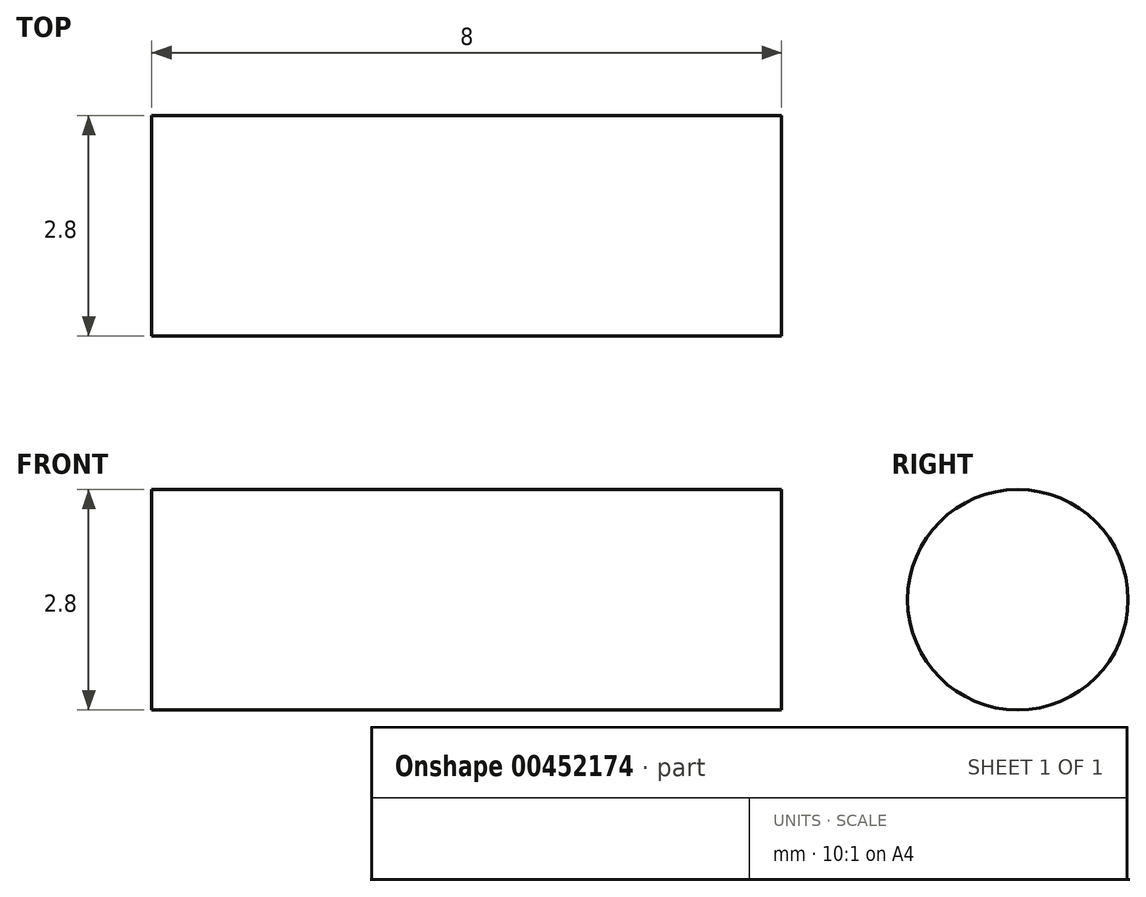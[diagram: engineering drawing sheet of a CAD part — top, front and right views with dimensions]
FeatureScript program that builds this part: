
annotation { "Feature Type Name" : "Feature", "Feature Type Description" : "" }
export const myFeature = defineFeature(function(context is Context, id is Id, definition is map)
    precondition{}
    {
        {
            var Q0;
            Q0=qCreatedBy(makeId("Right.planeOp"),FACE);
            var sketch = newSketch(context, id + "F0", { "sketchPlane" : qUnion([Q0])});
            skCircle(sketch, "E0", {"center": v(0, 0) * mm, "radius": 1.4 * mm});
            skSolve(sketch);
        }
        {
            var Q0;
            Q0 = qSketchRegion(id + "F0", true);
            extrude(context, id + "F1", {"entities" : qUnion([Q0]), "depth" : 8 * mm});
        }
    });
